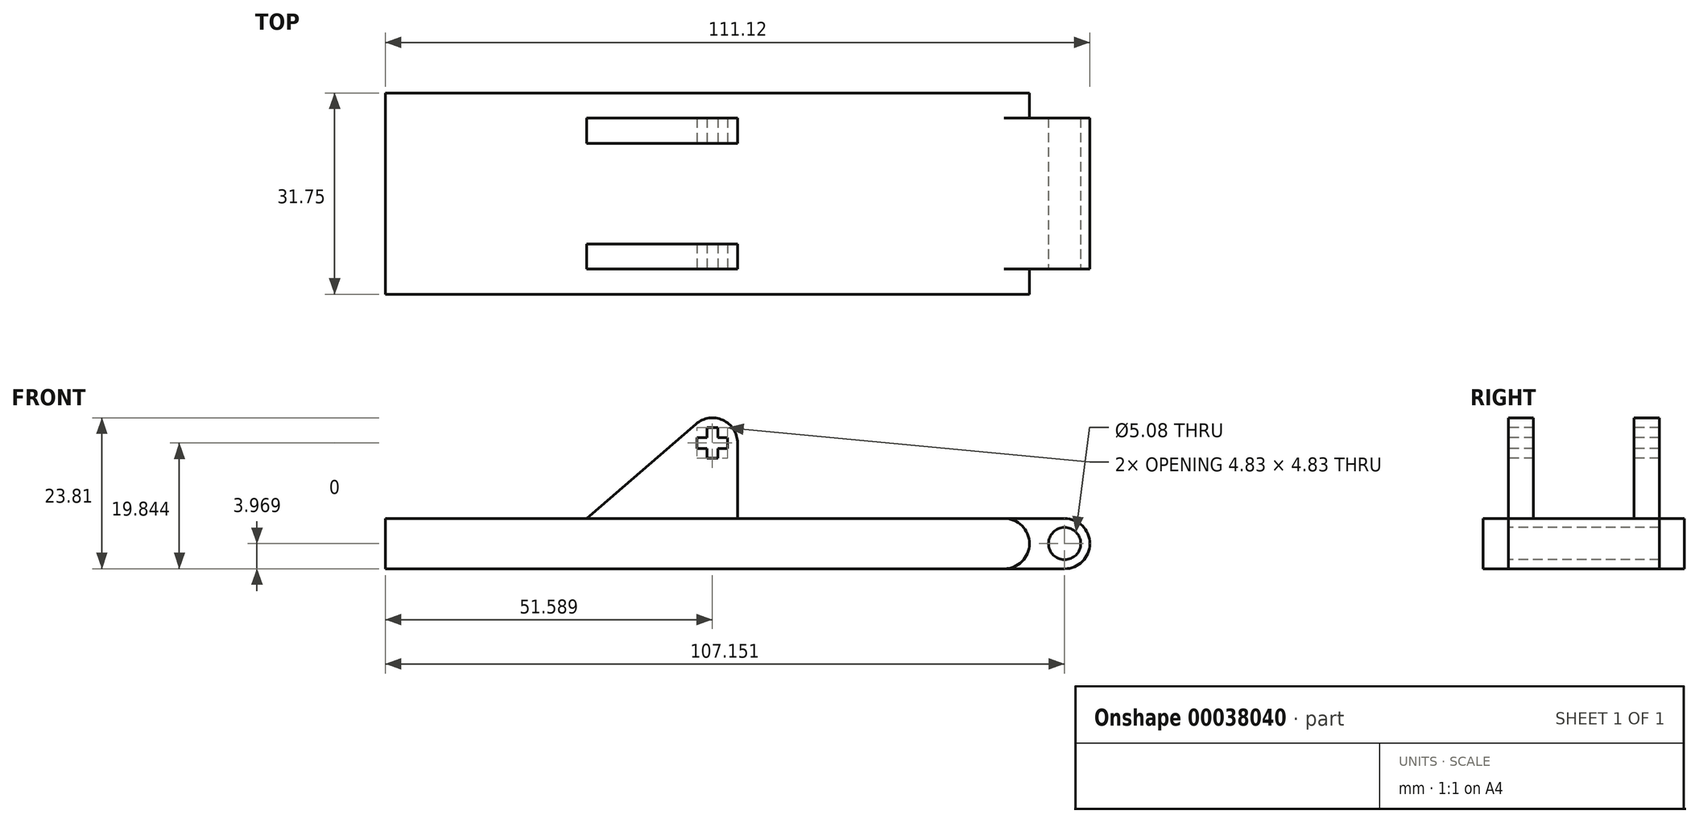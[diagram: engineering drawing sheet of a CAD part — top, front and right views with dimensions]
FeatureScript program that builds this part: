
annotation { "Feature Type Name" : "Feature", "Feature Type Description" : "" }
export const myFeature = defineFeature(function(context is Context, id is Id, definition is map)
    precondition{}
    {
        {
            var Q0;
            Q0=qCreatedBy(makeId("Top.planeOp"),FACE);
            var sketch = newSketch(context, id + "F0", { "sketchPlane" : qUnion([Q0])});
            skLineSegment(sketch, "E0.bottom", {"start": v(0, 0) * mm, "end": v(-9.53, 0) * mm});
            skLineSegment(sketch, "E0.top", {"start": v(0, -23.81) * mm, "end": v(-9.52, -23.81) * mm});
            skLineSegment(sketch, "E0.left", {"start": v(0, 0) * mm, "end": v(0, -23.81) * mm});
            skLineSegment(sketch, "E0.right", {"start": v(-9.53, 0) * mm, "end": v(-9.52, -23.81) * mm});
            skLineSegment(sketch, "E1.bottom", {"start": v(-9.53, 3.97) * mm, "end": v(-111.12, 3.97) * mm});
            skLineSegment(sketch, "E1.top", {"start": v(-9.52, -27.78) * mm, "end": v(-111.12, -27.78) * mm});
            skLineSegment(sketch, "E1.right", {"start": v(-111.12, 3.97) * mm, "end": v(-111.12, -27.78) * mm});
            skLineSegment(sketch, "E2", {"start": v(-9.53, 0) * mm, "end": v(-9.53, 3.97) * mm});
            skLineSegment(sketch, "E3", {"start": v(-9.52, -23.81) * mm, "end": v(-9.52, -27.78) * mm});
            skSolve(sketch);
        }
        {
            var Q0;
            Q0 = qSketchRegion(id + "F0", true);
            extrude(context, id + "F1", {"entities" : qUnion([Q0]), "depth" : 7.94 * mm});
        }
        {
            var Q0;
            Q0=makeQuery(id+"F1.opExtrude","CAP_EDGE",EDGE,{"disambiguationData":[OSD([sQuery(id+"F0.wireOp",EDGE,"E3")])],"isStart":false});
            var Q1;
            Q1=makeQuery(id+"F1.opExtrude","CAP_EDGE",EDGE,{"disambiguationData":[OSD([sQuery(id+"F0.wireOp",EDGE,"E3")])],"isStart":true});
            var Q2;
            Q2=makeQuery(id+"F1.opExtrude","CAP_EDGE",EDGE,{"disambiguationData":[OSD([sQuery(id+"F0.wireOp",EDGE,"E0.left")])],"isStart":false});
            var Q3;
            Q3=makeQuery(id+"F1.opExtrude","CAP_EDGE",EDGE,{"disambiguationData":[OSD([sQuery(id+"F0.wireOp",EDGE,"E0.left")])],"isStart":true});
            var Q4;
            Q4=makeQuery(id+"F1.opExtrude","CAP_EDGE",EDGE,{"disambiguationData":[OSD([sQuery(id+"F0.wireOp",EDGE,"E2")])],"isStart":false});
            var Q5;
            Q5=makeQuery(id+"F1.opExtrude","CAP_EDGE",EDGE,{"disambiguationData":[OSD([sQuery(id+"F0.wireOp",EDGE,"E2")])],"isStart":true});
            fillet(context, id + "F2", {"entities" : qUnion([Q0, Q1, Q2, Q3, Q4, Q5]), "radius" : 3.97 * mm, "tangentPropagation" : true, "allowEdgeOverflow" : false});
        }
        {
            var Q0;
            Q0=makeQuery(id+"F1.opExtrude","CAP_FACE",FACE,{"disambiguationData":[OSD([sQuery(id+"F0.wireOp",EDGE,"E0.bottom"),sQuery(id+"F0.wireOp",EDGE,"E0.top"),sQuery(id+"F0.wireOp",EDGE,"E0.left"),sQuery(id+"F0.wireOp",EDGE,"E1.bottom"),sQuery(id+"F0.wireOp",EDGE,"E1.top"),sQuery(id+"F0.wireOp",EDGE,"E1.right"),sQuery(id+"F0.wireOp",EDGE,"E2"),sQuery(id+"F0.wireOp",EDGE,"E3")])],"isStart":false});
            var sketch = newSketch(context, id + "F3", { "sketchPlane" : qUnion([Q0])});
            skLineSegment(sketch, "E4", {"start": v(-3.97, -11.9) * mm, "end": v(-55.56, -11.9) * mm, "construction": true});
            skPoint(sketch, "E4.endSnap0", {"position": v(-3.97, -11.9) * mm});
            skLineSegment(sketch, "E5", {"start": v(-55.56, -3.97) * mm, "end": v(-55.56, -19.84) * mm, "construction": true});
            skLineSegment(sketch, "E6.bottom", {"start": v(-55.56, -19.84) * mm, "end": v(-79.38, -19.84) * mm});
            skLineSegment(sketch, "E6.top", {"start": v(-55.56, -23.81) * mm, "end": v(-79.38, -23.81) * mm});
            skLineSegment(sketch, "E6.left", {"start": v(-55.56, -19.84) * mm, "end": v(-55.56, -23.81) * mm});
            skLineSegment(sketch, "E6.right", {"start": v(-79.38, -19.84) * mm, "end": v(-79.38, -23.81) * mm});
            skLineSegment(sketch, "E7.bottom", {"start": v(-55.56, -3.97) * mm, "end": v(-79.38, -3.97) * mm});
            skLineSegment(sketch, "E7.top", {"start": v(-55.56, 0) * mm, "end": v(-79.38, 0) * mm});
            skLineSegment(sketch, "E7.left", {"start": v(-55.56, -3.97) * mm, "end": v(-55.56, 0) * mm});
            skLineSegment(sketch, "E7.right", {"start": v(-79.38, -3.97) * mm, "end": v(-79.38, 0) * mm});
            skSolve(sketch);
        }
        {
            var Q0;
            Q0 = qSketchRegion(id + "F3", true);
            extrude(context, id + "F4", {"entities" : qUnion([Q0]), "operationType" : NewBodyOperationType.ADD, "depth" : 15.88 * mm});
        }
        {
            var Q0;
            Q0=makeQuery(id+"F4.boolean.opBoolean","MERGE",FACE,{"derivedFrom":[makeQuery(id+"F1.opExtrude","SWEPT_FACE",FACE,{"disambiguationData":[OSD([sQuery(id+"F0.wireOp",EDGE,"E1.top")])]}),makeQuery(id+"F4.opExtrude","SWEPT_FACE",FACE,{"disambiguationData":[OSD([sQuery(id+"F3.wireOp",EDGE,"E6.top")])]})]});
            var sketch = newSketch(context, id + "F5", { "sketchPlane" : qUnion([Q0])});
            skLineSegment(sketch, "E8.bottom", {"start": v(-79.38, 7.94) * mm, "end": v(-55.56, 7.94) * mm, "construction": true});
            skLineSegment(sketch, "E8.top", {"start": v(-79.38, 23.81) * mm, "end": v(-55.56, 23.81) * mm});
            skLineSegment(sketch, "E8.left", {"start": v(-79.38, 7.94) * mm, "end": v(-79.38, 23.81) * mm});
            skLineSegment(sketch, "E8.right", {"start": v(-55.56, 7.94) * mm, "end": v(-55.56, 23.81) * mm});
            skLineSegment(sketch, "E9", {"start": v(-79.38, 7.94) * mm, "end": v(-62.13, 22.85) * mm});
            skArc(sketch, "E10", {"start": v(-55.56, 19.84) * mm, "mid": v(-57.88, 23.45) * mm, "end": v(-62.13, 22.85) * mm});
            skLineSegment(sketch, "E11.rect.bottom", {"start": v(-58.69, 17.43) * mm, "end": v(-60.38, 17.43) * mm});
            skLineSegment(sketch, "E11.rect.top", {"start": v(-58.69, 22.26) * mm, "end": v(-60.38, 22.26) * mm});
            skLineSegment(sketch, "E11.rect.left", {"start": v(-58.69, 17.43) * mm, "end": v(-58.69, 22.26) * mm});
            skLineSegment(sketch, "E11.rect.right", {"start": v(-60.38, 17.43) * mm, "end": v(-60.38, 22.26) * mm});
            skLineSegment(sketch, "E12.rect.bottom", {"start": v(-61.94, 19) * mm, "end": v(-57.12, 19) * mm});
            skLineSegment(sketch, "E12.rect.top", {"start": v(-61.94, 20.69) * mm, "end": v(-57.12, 20.69) * mm});
            skLineSegment(sketch, "E12.rect.left", {"start": v(-61.94, 19) * mm, "end": v(-61.94, 20.69) * mm});
            skLineSegment(sketch, "E12.rect.right", {"start": v(-57.12, 19) * mm, "end": v(-57.12, 20.69) * mm});
            skCircle(sketch, "E13", {"center": v(-3.97, 3.97) * mm, "radius": 2.54 * mm});
            skSolve(sketch);
        }
        {
            var Q0;
            Q0 = qSketchRegion(id + "F5", true);
            var Q1;
            Q1=makeQuery(id+"F4.boolean.opBoolean","MERGE",FACE,{"derivedFrom":[makeQuery(id+"F1.opExtrude","SWEPT_FACE",FACE,{"disambiguationData":[OSD([sQuery(id+"F0.wireOp",EDGE,"E1.bottom")])]}),makeQuery(id+"F4.opExtrude","SWEPT_FACE",FACE,{"disambiguationData":[OSD([sQuery(id+"F3.wireOp",EDGE,"E7.top")])]})]});
            extrude(context, id + "F6", {"entities" : qUnion([Q0]), "operationType" : NewBodyOperationType.REMOVE, "endBound" : BoundingType.UP_TO_SURFACE, "oppositeDirection" : true, "endBoundEntityFace" : qUnion([Q1]), "depth" : 25.4 * mm});
        }
    });
